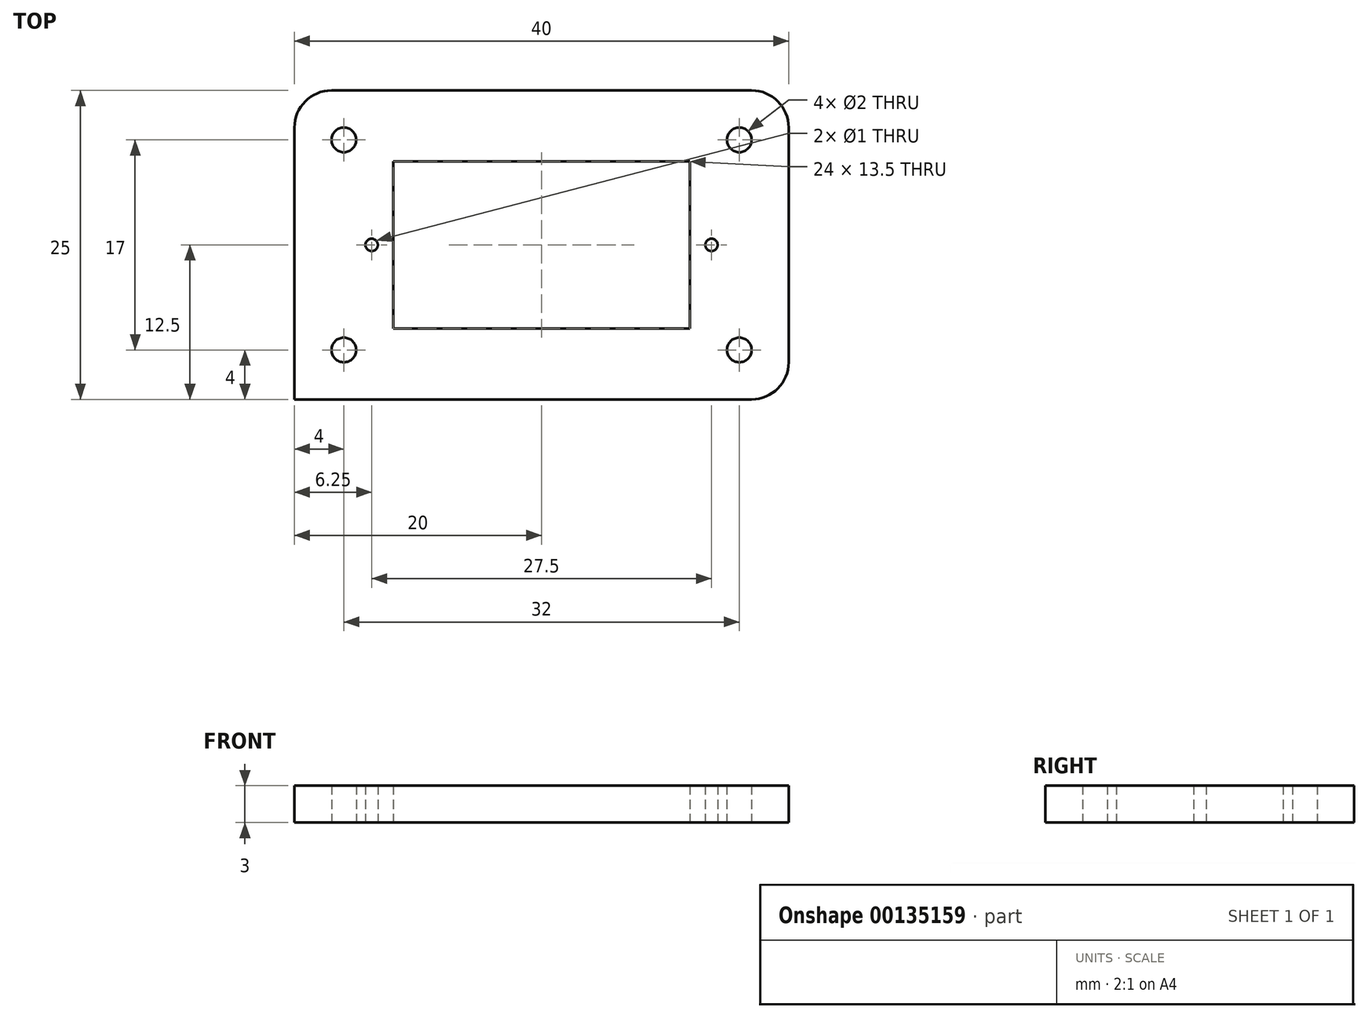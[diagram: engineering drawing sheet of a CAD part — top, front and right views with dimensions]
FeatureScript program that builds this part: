
annotation { "Feature Type Name" : "Feature", "Feature Type Description" : "" }
export const myFeature = defineFeature(function(context is Context, id is Id, definition is map)
    precondition{}
    {
        {
            var Q0;
            Q0=qCreatedBy(makeId("Top.planeOp"),FACE);
            var sketch = newSketch(context, id + "F0", { "sketchPlane" : qUnion([Q0])});
            skLineSegment(sketch, "E0.bottom", {"start": v(12, -6.75) * mm, "end": v(-12, -6.75) * mm});
            skLineSegment(sketch, "E0.top", {"start": v(12, 6.75) * mm, "end": v(-12, 6.75) * mm});
            skLineSegment(sketch, "E0.left", {"start": v(12, -6.75) * mm, "end": v(12, 6.75) * mm});
            skLineSegment(sketch, "E0.right", {"start": v(-12, -6.75) * mm, "end": v(-12, 6.75) * mm});
            skPoint(sketch, "E0.middle", {"position": v(0, 0) * mm});
            skLineSegment(sketch, "E1.bottom", {"start": v(13.75, 0) * mm, "end": v(-13.75, 0) * mm, "construction": true});
            skLineSegment(sketch, "E1.top", {"start": v(13.75, 0) * mm, "end": v(-13.75, 0) * mm, "construction": true});
            skLineSegment(sketch, "E1.left", {"start": v(13.75, 0) * mm, "end": v(13.75, 0) * mm});
            skLineSegment(sketch, "E1.right", {"start": v(-13.75, 0) * mm, "end": v(-13.75, 0) * mm});
            skLineSegment(sketch, "E2.bottom", {"start": v(20, 12.5) * mm, "end": v(-20, 12.5) * mm});
            skLineSegment(sketch, "E2.top", {"start": v(20, -12.5) * mm, "end": v(-20, -12.5) * mm});
            skLineSegment(sketch, "E2.left", {"start": v(20, 12.5) * mm, "end": v(20, -12.5) * mm});
            skLineSegment(sketch, "E2.right", {"start": v(-20, 12.5) * mm, "end": v(-20, -12.5) * mm});
            skPoint(sketch, "E3.middle", {"position": v(-20, 12.5) * mm});
            skLineSegment(sketch, "E4.bottom", {"start": v(-20, 12.5) * mm, "end": v(-16, 12.5) * mm, "construction": true});
            skLineSegment(sketch, "E4.top", {"start": v(-20, 8.5) * mm, "end": v(-16, 8.5) * mm, "construction": true});
            skLineSegment(sketch, "E4.left", {"start": v(-20, 12.5) * mm, "end": v(-20, 8.5) * mm, "construction": true});
            skLineSegment(sketch, "E4.right", {"start": v(-16, 12.5) * mm, "end": v(-16, 8.5) * mm, "construction": true});
            skLineSegment(sketch, "E5.bottom", {"start": v(20, 12.5) * mm, "end": v(16, 12.5) * mm});
            skLineSegment(sketch, "E5.top", {"start": v(20, 8.5) * mm, "end": v(16, 8.5) * mm, "construction": true});
            skLineSegment(sketch, "E5.left", {"start": v(20, 12.5) * mm, "end": v(20, 8.5) * mm, "construction": true});
            skLineSegment(sketch, "E5.right", {"start": v(16, 12.5) * mm, "end": v(16, 8.5) * mm, "construction": true});
            skLineSegment(sketch, "E6.bottom", {"start": v(20, -12.5) * mm, "end": v(16, -12.5) * mm});
            skLineSegment(sketch, "E6.top", {"start": v(20, -8.5) * mm, "end": v(16, -8.5) * mm, "construction": true});
            skLineSegment(sketch, "E6.left", {"start": v(20, -12.5) * mm, "end": v(20, -8.5) * mm});
            skLineSegment(sketch, "E6.right", {"start": v(16, -12.5) * mm, "end": v(16, -8.5) * mm, "construction": true});
            skLineSegment(sketch, "E7.bottom", {"start": v(-20, -12.5) * mm, "end": v(-16, -12.5) * mm});
            skLineSegment(sketch, "E7.top", {"start": v(-20, -8.5) * mm, "end": v(-16, -8.5) * mm, "construction": true});
            skLineSegment(sketch, "E7.left", {"start": v(-20, -12.5) * mm, "end": v(-20, -8.5) * mm});
            skLineSegment(sketch, "E7.right", {"start": v(-16, -12.5) * mm, "end": v(-16, -8.5) * mm, "construction": true});
            skCircle(sketch, "E8", {"center": v(-16, 8.5) * mm, "radius": 1 * mm});
            skCircle(sketch, "E9", {"center": v(16, 8.5) * mm, "radius": 1 * mm});
            skCircle(sketch, "E10", {"center": v(16, -8.5) * mm, "radius": 1 * mm});
            skCircle(sketch, "E11", {"center": v(-16, -8.5) * mm, "radius": 1 * mm});
            skCircle(sketch, "E12", {"center": v(-13.75, 0) * mm, "radius": 0.5 * mm});
            skCircle(sketch, "E13", {"center": v(13.75, 0) * mm, "radius": 0.5 * mm});
            skSolve(sketch);
        }
        {
            var Q0;
            Q0=makeQuery(id+"F0.imprint","IMPRINT",FACE,{"disambiguationData":[TD([[makeQuery(id+"F0.imprint","IMPRINT",EDGE,{"derivedFrom":sQuery(id+"F0.wireOp",EDGE,"E0.bottom")}),1.0]])]});
            extrude(context, id + "F1", {"entities" : qUnion([Q0]), "depth" : 3 * mm});
        }
        {
            var Q0;
            Q0=makeQuery(id+"F1.opExtrude","SWEPT_EDGE",EDGE,{"disambiguationData":[OSD([sQuery(id+"F0.wireOp",EDGE,"E6.bottom"),sQuery(id+"F0.wireOp",EDGE,"E6.left")])]});
            var Q1;
            Q1=makeQuery(id+"F1.opExtrude","SWEPT_EDGE",EDGE,{"disambiguationData":[OSD([sQuery(id+"F0.wireOp",EDGE,"E7.bottom"),sQuery(id+"F0.wireOp",EDGE,"E7.left")])]});
            var Q2;
            Q2=makeQuery(id+"F1.opExtrude","SWEPT_EDGE",EDGE,{"disambiguationData":[OSD([sQuery(id+"F0.wireOp",EDGE,"E2.left"),sQuery(id+"F0.wireOp",EDGE,"E5.bottom")])]});
            var Q3;
            Q3=makeQuery(id+"F1.opExtrude","SWEPT_EDGE",EDGE,{"disambiguationData":[OSD([sQuery(id+"F0.wireOp",EDGE,"E2.bottom"),sQuery(id+"F0.wireOp",EDGE,"E2.right")])]});
            fillet(context, id + "F2", {"entities" : qUnion([Q0, Q1, Q2, Q3]), "radius" : 3 * mm, "tangentPropagation" : true, "allowEdgeOverflow" : false});
        }
    });
